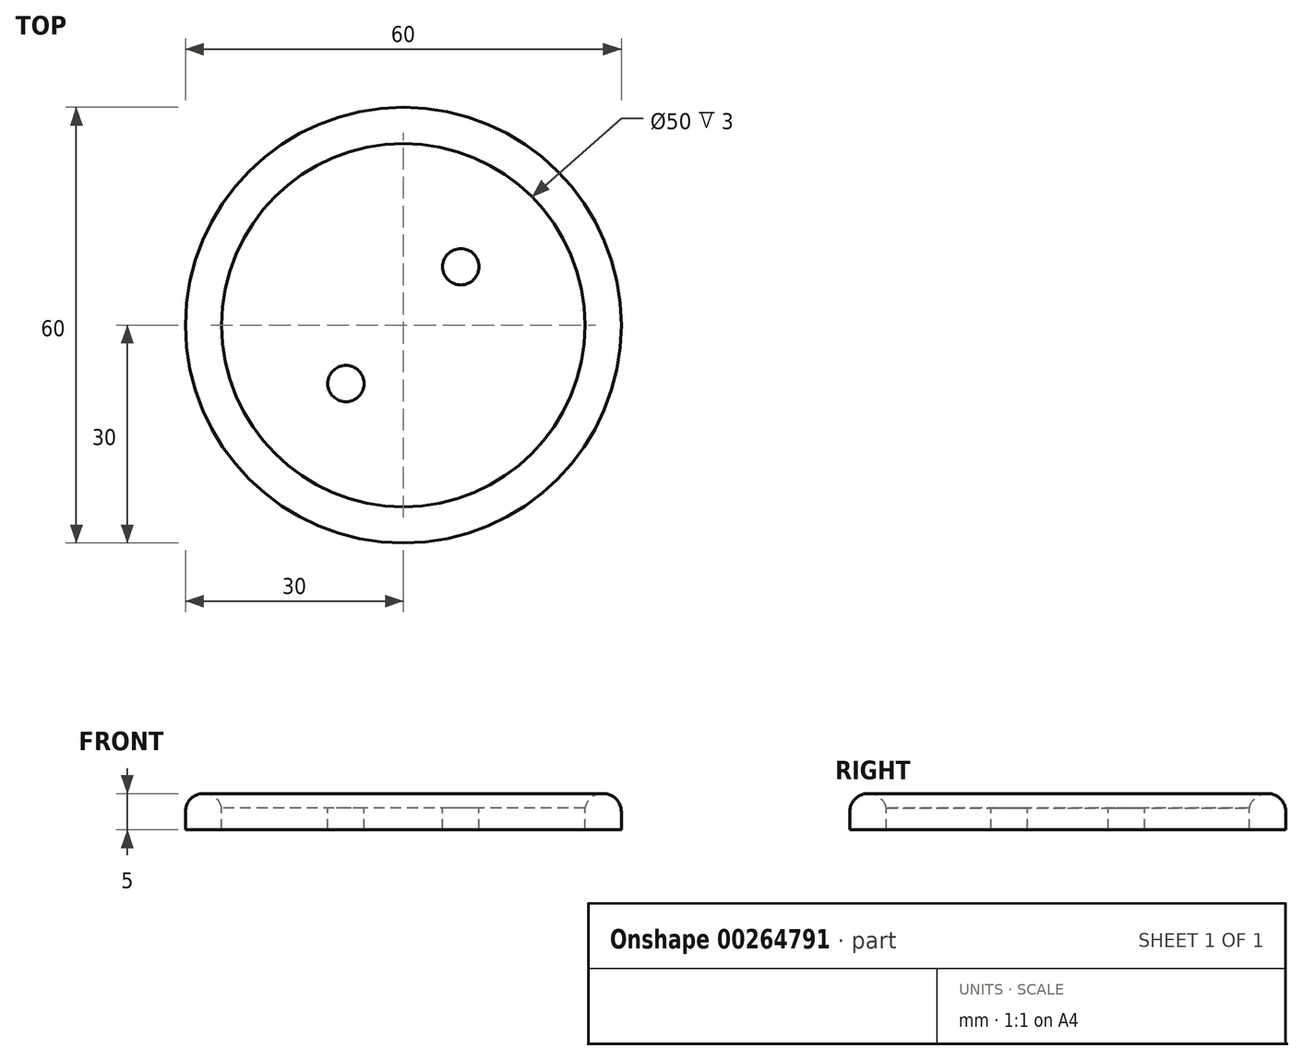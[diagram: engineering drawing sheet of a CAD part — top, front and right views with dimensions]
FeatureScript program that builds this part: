
annotation { "Feature Type Name" : "Feature", "Feature Type Description" : "" }
export const myFeature = defineFeature(function(context is Context, id is Id, definition is map)
    precondition{}
    {
        {
            var Q0;
            Q0=qCreatedBy(makeId("Top.planeOp"),FACE);
            var sketch = newSketch(context, id + "F0", { "sketchPlane" : qUnion([Q0])});
            skCircle(sketch, "E0", {"center": v(0, 0) * mm, "radius": 25 * mm});
            skCircle(sketch, "E1", {"center": v(0, 0) * mm, "radius": 30 * mm});
            skLineSegment(sketch, "E2", {"start": v(-25, 0) * mm, "end": v(25, 0) * mm, "construction": true});
            skLineSegment(sketch, "E3", {"start": v(-30, 0) * mm, "end": v(30, 0) * mm, "construction": true});
            skSolve(sketch);
        }
        {
            var Q0;
            Q0=makeQuery(id+"F0.imprint","IMPRINT",FACE,{"disambiguationData":[TD([[makeQuery(id+"F0.imprint","IMPRINT",EDGE,{"derivedFrom":sQuery(id+"F0.wireOp",EDGE,"E0")}),1.0]])]});
            extrude(context, id + "F1", {"entities" : qUnion([Q0]), "depth" : 3 * mm, "offsetDistance" : 25 * mm});
        }
        {
            var Q0;
            Q0=makeQuery(id+"F0.imprint","IMPRINT",FACE,{"disambiguationData":[TD([[makeQuery(id+"F0.imprint","IMPRINT",EDGE,{"derivedFrom":sQuery(id+"F0.wireOp",EDGE,"E0")}),-1.0]])]});
            extrude(context, id + "F2", {"entities" : qUnion([Q0]), "operationType" : NewBodyOperationType.ADD, "depth" : 5 * mm, "offsetDistance" : 25 * mm});
        }
        {
            var Q0;
            Q0=makeQuery(id+"F2.opExtrude","CAP_FACE",FACE,{"disambiguationData":[OSD([sQuery(id+"F0.wireOp",EDGE,"E0"),sQuery(id+"F0.wireOp",EDGE,"E1")])],"isStart":false});
            fillet(context, id + "F3", {"entities" : qUnion([Q0]), "radius" : 2.5 * mm, "tangentPropagation" : true, "allowEdgeOverflow" : false});
        }
        {
            var Q0;
            Q0=makeQuery(id+"F1.opExtrude","CAP_FACE",FACE,{"disambiguationData":[OSD([sQuery(id+"F0.wireOp",EDGE,"E0")])],"isStart":false});
            var sketch = newSketch(context, id + "F4", { "sketchPlane" : qUnion([Q0])});
            skLineSegment(sketch, "E4", {"start": v(0, 10.65) * mm, "end": v(0, -12.17) * mm, "construction": true});
            skLineSegment(sketch, "E5", {"start": v(-10.65, 0) * mm, "end": v(11.36, 0) * mm, "construction": true});
            skCircle(sketch, "E6", {"center": v(-7.9, 8.05) * mm, "radius": 2.5 * mm});
            skLineSegment(sketch, "E7", {"start": v(-10.4, 7.95) * mm, "end": v(-5.4, 7.95) * mm, "construction": true});
            skCircle(sketch, "E8.MirrorC", {"center": v(7.9, 8.05) * mm, "radius": 2.5 * mm});
            skCircle(sketch, "E9.MirrorC", {"center": v(-7.9, -8.05) * mm, "radius": 2.5 * mm});
            skCircle(sketch, "E10.MirrorC", {"center": v(7.9, -8.05) * mm, "radius": 2.5 * mm});
            skSolve(sketch);
        }
        {
            var Q0;
            Q0=makeQuery(id+"F4.imprint","IMPRINT",FACE,{"disambiguationData":[TD([[makeQuery(id+"F4.imprint","IMPRINT",EDGE,{"derivedFrom":sQuery(id+"F4.wireOp",EDGE,"E6")}),1.0]])]});
            var Q1;
            Q1=makeQuery(id+"F4.imprint","IMPRINT",FACE,{"disambiguationData":[TD([[makeQuery(id+"F4.imprint","IMPRINT",EDGE,{"derivedFrom":sQuery(id+"F4.wireOp",EDGE,"E10.MirrorC")}),1.0]])]});
            var Q2;
            Q2=makeQuery(id+"F4.imprint","IMPRINT",FACE,{"disambiguationData":[TD([[makeQuery(id+"F4.imprint","IMPRINT",EDGE,{"derivedFrom":sQuery(id+"F4.wireOp",EDGE,"E8.MirrorC")}),-1.0]])]});
            var Q3;
            Q3=makeQuery(id+"F4.imprint","IMPRINT",FACE,{"disambiguationData":[TD([[makeQuery(id+"F4.imprint","IMPRINT",EDGE,{"derivedFrom":sQuery(id+"F4.wireOp",EDGE,"E9.MirrorC")}),-1.0]])]});
            extrude(context, id + "F5", {"entities" : qUnion([Q0, Q1, Q2, Q3]), "operationType" : NewBodyOperationType.REMOVE, "oppositeDirection" : true, "depth" : 25 * mm, "offsetDistance" : 25 * mm});
        }
    });
